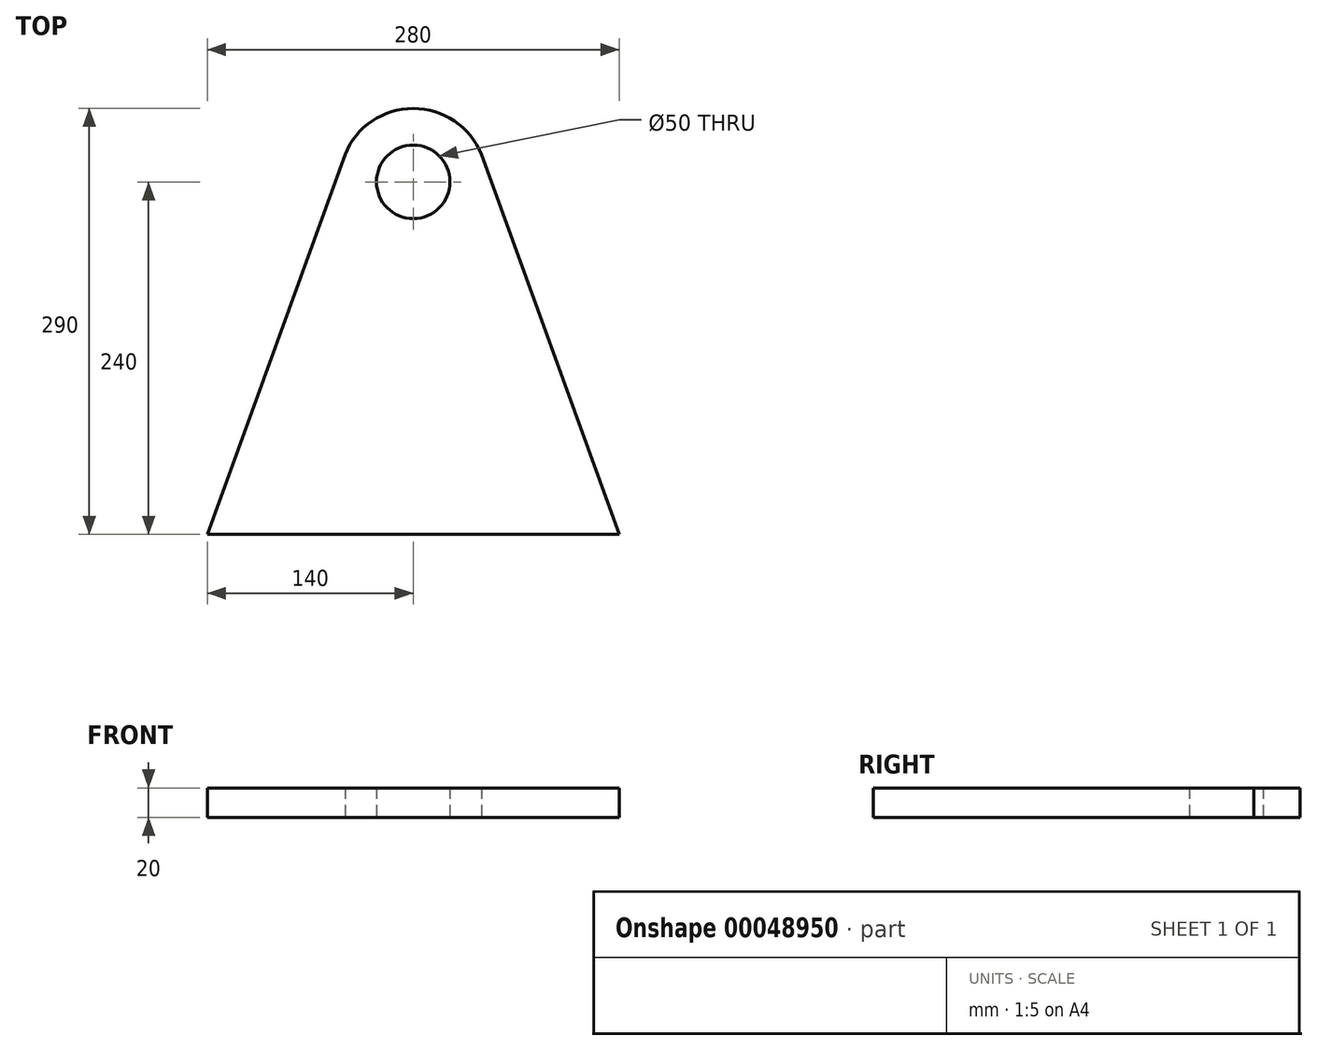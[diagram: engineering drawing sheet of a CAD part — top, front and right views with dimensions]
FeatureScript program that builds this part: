
annotation { "Feature Type Name" : "Feature", "Feature Type Description" : "" }
export const myFeature = defineFeature(function(context is Context, id is Id, definition is map)
    precondition{}
    {
        {
            var Q0;
            Q0=qCreatedBy(makeId("Top.planeOp"),FACE);
            var sketch = newSketch(context, id + "F0", { "sketchPlane" : qUnion([Q0])});
            skLineSegment(sketch, "E0", {"start": v(0, 0) * mm, "end": v(140, 0) * mm});
            skLineSegment(sketch, "E1", {"start": v(0, 0) * mm, "end": v(0, 240) * mm, "construction": true});
            skLineSegment(sketch, "E2", {"start": v(0, 240) * mm, "end": v(50, 240) * mm, "construction": true});
            skLineSegment(sketch, "E3", {"start": v(140, 0) * mm, "end": v(46.4, 258.65) * mm});
            skLineSegment(sketch, "E4.MirrorCS", {"start": v(0, 0) * mm, "end": v(-140, 0) * mm});
            skLineSegment(sketch, "E5.MirrorCS", {"start": v(-140, 0) * mm, "end": v(-46.4, 258.65) * mm});
            skCircle(sketch, "E6", {"center": v(0, 240) * mm, "radius": 50 * mm});
            skCircle(sketch, "E7", {"center": v(0, 240) * mm, "radius": 25 * mm});
            skSolve(sketch);
        }
        {
            var Q0;
            {var subQ5=sQuery(id+"F0.wireOp",EDGE,"E0");Q0=makeQuery(id+"F0.imprint","IMPRINT",FACE,{"disambiguationData":[TD([[makeQuery(id+"F0.imprint","IMPRINT",EDGE,{"derivedFrom":subQ5}),1.0]])]});}
            var Q1;
            Q1=makeQuery(id+"F0.imprint","IMPRINT",FACE,{"disambiguationData":[TD([[makeQuery(id+"F0.imprint","IMPRINT",EDGE,{"derivedFrom":sQuery(id+"F0.wireOp",EDGE,"E7")}),-1.0]])]});
            extrude(context, id + "F1", {"entities" : qUnion([Q0, Q1]), "depth" : 20 * mm});
        }
    });
